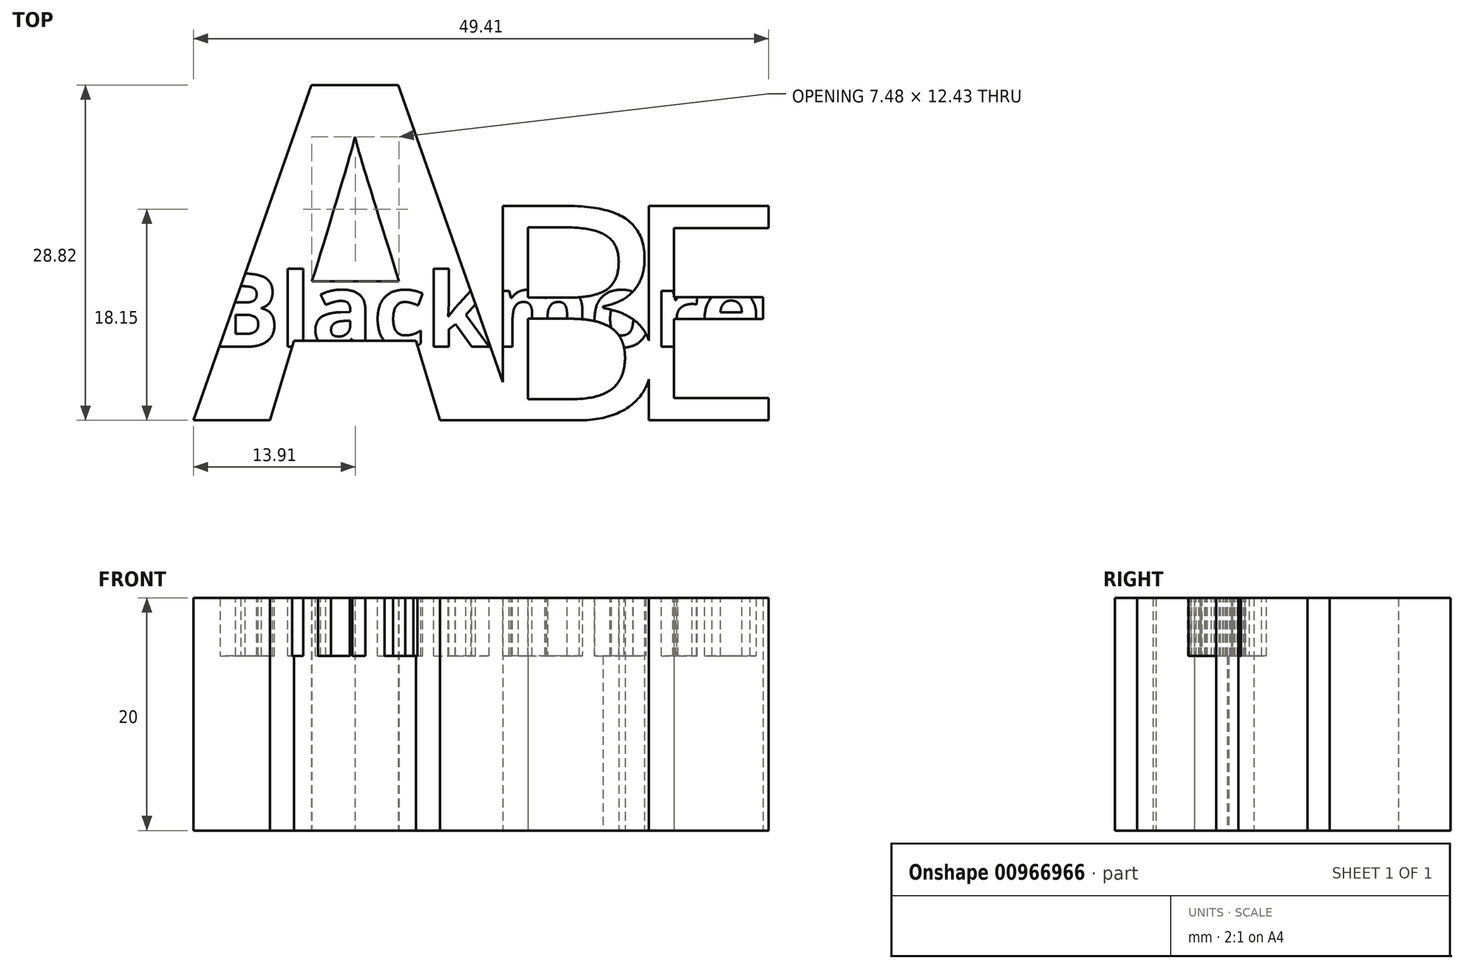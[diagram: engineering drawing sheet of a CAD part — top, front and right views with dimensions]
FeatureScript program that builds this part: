
annotation { "Feature Type Name" : "Feature", "Feature Type Description" : "" }
export const myFeature = defineFeature(function(context is Context, id is Id, definition is map)
    precondition{}
    {
        {
            var Q0;
            Q0=qCreatedBy(makeId("Top.planeOp"),FACE);
            var sketch = newSketch(context, id + "F0", { "sketchPlane" : qUnion([Q0])});
            skText(sketch, "E0", { "text": "A", "fontName": "OpenSans-Bold.ttf"});
            skText(sketch, "E1", { "text": "B", "fontName": "OpenSans-Regular.ttf"});
            skText(sketch, "E2", { "text": "E", "fontName": "OpenSans-Regular.ttf"});
            const initialGuessF0  = {"E0": [-0.05846, -0.02223, 1, 0, 0.02895], "E1": [-0.03441, -0.02223, 1, 0, 0.0186], "E2": [-0.02187, -0.02223, 1, 0, 0.0186]};
            skSetInitialGuess(sketch, initialGuessF0);
            skSolve(sketch);
        }
        {
            var Q0;
            Q0 = qSketchRegion(id + "F0", true);
            extrude(context, id + "F1", {"entities" : qUnion([Q0]), "depth" : 20 * mm, "offsetDistance" : 25 * mm});
        }
        {
            var Q0;
            Q0=makeQuery(id+"F1.opExtrude","CAP_FACE",FACE,{"disambiguationData":[OSD([sQuery(id+"F0.wireOp",EDGE,"E0.sketch_text.stroke-0"),sQuery(id+"F0.wireOp",EDGE,"E0.sketch_text.stroke-1"),sQuery(id+"F0.wireOp",EDGE,"E0.sketch_text.stroke-2"),sQuery(id+"F0.wireOp",EDGE,"E0.sketch_text.stroke-3"),sQuery(id+"F0.wireOp",EDGE,"E0.sketch_text.stroke-4"),sQuery(id+"F0.wireOp",EDGE,"E0.sketch_text.stroke-5"),sQuery(id+"F0.wireOp",EDGE,"E0.sketch_text.stroke-6"),sQuery(id+"F0.wireOp",EDGE,"E0.sketch_text.stroke-7"),sQuery(id+"F0.wireOp",EDGE,"E0.sketch_text.stroke-8"),sQuery(id+"F0.wireOp",EDGE,"E0.sketch_text.stroke-9"),sQuery(id+"F0.wireOp",EDGE,"E0.sketch_text.stroke-10"),sQuery(id+"F0.wireOp",EDGE,"E0.sketch_text.stroke-11"),sQuery(id+"F0.wireOp",EDGE,"E1.sketch_text.stroke-0"),sQuery(id+"F0.wireOp",EDGE,"E1.sketch_text.stroke-1"),sQuery(id+"F0.wireOp",EDGE,"E1.sketch_text.stroke-2"),sQuery(id+"F0.wireOp",EDGE,"E1.sketch_text.stroke-3"),sQuery(id+"F0.wireOp",EDGE,"E1.sketch_text.stroke-4"),sQuery(id+"F0.wireOp",EDGE,"E1.sketch_text.stroke-5"),sQuery(id+"F0.wireOp",EDGE,"E1.sketch_text.stroke-6"),sQuery(id+"F0.wireOp",EDGE,"E1.sketch_text.stroke-7"),sQuery(id+"F0.wireOp",EDGE,"E1.sketch_text.stroke-8"),sQuery(id+"F0.wireOp",EDGE,"E1.sketch_text.stroke-9"),sQuery(id+"F0.wireOp",EDGE,"E1.sketch_text.stroke-10"),sQuery(id+"F0.wireOp",EDGE,"E1.sketch_text.stroke-11"),sQuery(id+"F0.wireOp",EDGE,"E1.sketch_text.stroke-12"),sQuery(id+"F0.wireOp",EDGE,"E1.sketch_text.stroke-13"),sQuery(id+"F0.wireOp",EDGE,"E1.sketch_text.stroke-14"),sQuery(id+"F0.wireOp",EDGE,"E1.sketch_text.stroke-15"),sQuery(id+"F0.wireOp",EDGE,"E1.sketch_text.stroke-16"),sQuery(id+"F0.wireOp",EDGE,"E1.sketch_text.stroke-17"),sQuery(id+"F0.wireOp",EDGE,"E1.sketch_text.stroke-18"),sQuery(id+"F0.wireOp",EDGE,"E1.sketch_text.stroke-19"),sQuery(id+"F0.wireOp",EDGE,"E1.sketch_text.stroke-20"),sQuery(id+"F0.wireOp",EDGE,"E1.sketch_text.stroke-21"),sQuery(id+"F0.wireOp",EDGE,"E1.sketch_text.stroke-22"),sQuery(id+"F0.wireOp",EDGE,"E1.sketch_text.stroke-23"),sQuery(id+"F0.wireOp",EDGE,"E1.sketch_text.stroke-24"),sQuery(id+"F0.wireOp",EDGE,"E2.sketch_text.stroke-0"),sQuery(id+"F0.wireOp",EDGE,"E2.sketch_text.stroke-1"),sQuery(id+"F0.wireOp",EDGE,"E2.sketch_text.stroke-2"),sQuery(id+"F0.wireOp",EDGE,"E2.sketch_text.stroke-3"),sQuery(id+"F0.wireOp",EDGE,"E2.sketch_text.stroke-4"),sQuery(id+"F0.wireOp",EDGE,"E2.sketch_text.stroke-5"),sQuery(id+"F0.wireOp",EDGE,"E2.sketch_text.stroke-6"),sQuery(id+"F0.wireOp",EDGE,"E2.sketch_text.stroke-7"),sQuery(id+"F0.wireOp",EDGE,"E2.sketch_text.stroke-8"),sQuery(id+"F0.wireOp",EDGE,"E2.sketch_text.stroke-9"),sQuery(id+"F0.wireOp",EDGE,"E2.sketch_text.stroke-10"),sQuery(id+"F0.wireOp",EDGE,"E2.sketch_text.stroke-11")])],"isStart":false});
            var sketch = newSketch(context, id + "F2", { "sketchPlane" : qUnion([Q0])});
            skText(sketch, "E3", { "text": "Blackmore", "fontName": "OpenSans-Bold.ttf"});
            const initialGuessF2  = {"E3": [-0.05696, -0.0159, 1, 0, 0.00634]};
            skSetInitialGuess(sketch, initialGuessF2);
            skSolve(sketch);
        }
        {
            var Q0;
            Q0 = qSketchRegion(id + "F2", true);
            extrude(context, id + "F3", {"entities" : qUnion([Q0]), "operationType" : NewBodyOperationType.REMOVE, "oppositeDirection" : true, "depth" : 5 * mm, "offsetDistance" : 25 * mm});
        }
    });
